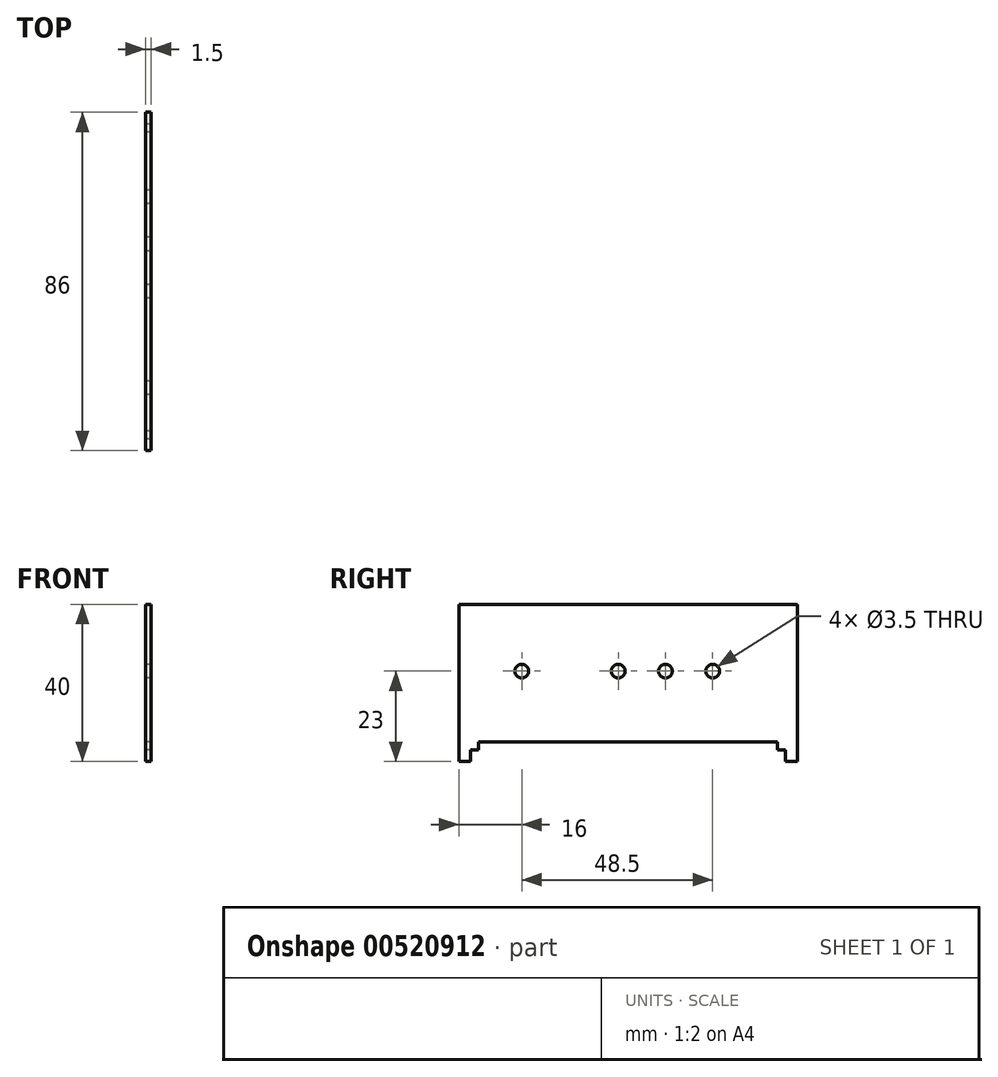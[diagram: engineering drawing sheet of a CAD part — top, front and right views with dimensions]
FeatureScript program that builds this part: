
annotation { "Feature Type Name" : "Feature", "Feature Type Description" : "" }
export const myFeature = defineFeature(function(context is Context, id is Id, definition is map)
    precondition{}
    {
        {
            var Q0;
            Q0=qCreatedBy(makeId("Right.planeOp"),FACE);
            var sketch = newSketch(context, id + "F0", { "sketchPlane" : qUnion([Q0])});
            skLineSegment(sketch, "E0", {"start": v(-43, 37) * mm, "end": v(-43, -3) * mm});
            skLineSegment(sketch, "E1", {"start": v(-43, -3) * mm, "end": v(-40, -3) * mm});
            skLineSegment(sketch, "E2", {"start": v(-40, -3) * mm, "end": v(-40, 0) * mm});
            skLineSegment(sketch, "E3", {"start": v(-40, 0) * mm, "end": v(-38, 0) * mm});
            skLineSegment(sketch, "E4", {"start": v(-38, 0) * mm, "end": v(-38, 2) * mm});
            skLineSegment(sketch, "E5", {"start": v(0, 2) * mm, "end": v(-38, 2) * mm});
            skLineSegment(sketch, "E6", {"start": v(-43, 37) * mm, "end": v(0, 37) * mm});
            skLineSegment(sketch, "E7.MirrorCS", {"start": v(43, -3) * mm, "end": v(40, -3) * mm});
            skLineSegment(sketch, "E8.MirrorCS", {"start": v(40, 0) * mm, "end": v(38, 0) * mm});
            skLineSegment(sketch, "E9.MirrorCS", {"start": v(40, -3) * mm, "end": v(40, 0) * mm});
            skLineSegment(sketch, "E10.MirrorCS", {"start": v(38, 0) * mm, "end": v(38, 2) * mm});
            skLineSegment(sketch, "E11.MirrorCS", {"start": v(0, 2) * mm, "end": v(38, 2) * mm});
            skLineSegment(sketch, "E12.MirrorCS", {"start": v(43, 37) * mm, "end": v(0, 37) * mm});
            skLineSegment(sketch, "E13.MirrorCS", {"start": v(43, 37) * mm, "end": v(43, -3) * mm});
            skCircle(sketch, "E14", {"center": v(-2.5, 20) * mm, "radius": 1.75 * mm});
            skCircle(sketch, "E15.1.0.0", {"center": v(9.5, 20) * mm, "radius": 1.75 * mm});
            skCircle(sketch, "E15.2.0.0", {"center": v(21.5, 20) * mm, "radius": 1.75 * mm});
            skLineSegment(sketch, "E15.direction1", {"start": v(-2.5, 20) * mm, "end": v(9.5, 20) * mm, "construction": true});
            skCircle(sketch, "E16.1.0.0", {"center": v(-27, 20) * mm, "radius": 1.75 * mm});
            skLineSegment(sketch, "E16.direction1", {"start": v(-2.5, 20) * mm, "end": v(-27, 20) * mm, "construction": true});
            skSolve(sketch);
        }
        {
            var Q0;
            Q0=makeQuery(id+"F0.imprint","IMPRINT",FACE,{"disambiguationData":[TD([[makeQuery(id+"F0.imprint","IMPRINT",EDGE,{"derivedFrom":sQuery(id+"F0.wireOp",EDGE,"E0")}),1.0]])]});
            extrude(context, id + "F1", {"entities" : qUnion([Q0]), "endBound" : BoundingType.SYMMETRIC, "depth" : 1.5 * mm, "offsetDistance" : 25 * mm});
        }
    });
